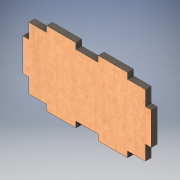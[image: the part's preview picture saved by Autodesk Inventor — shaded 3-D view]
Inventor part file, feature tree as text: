
AUTODESK INVENTOR PART (.ipt)
format: ipt  version: 2019 (Build 230136000, 136)  size: 237,056 bytes
history: native  units: mm
features: other x1, extrude x1, sketch x1
ambient origin geometry x8: Origin, YZ Plane, XZ Plane, XY Plane, X Axis, Y Axis, Z Axis, Center Point
bodies: Body1 (feature_tree)
feature tree (3):
  other  "Твердое тело1"
  extrude  "Выдавливание1"  Depth=20.0mm
  sketch  "Эскиз1"
